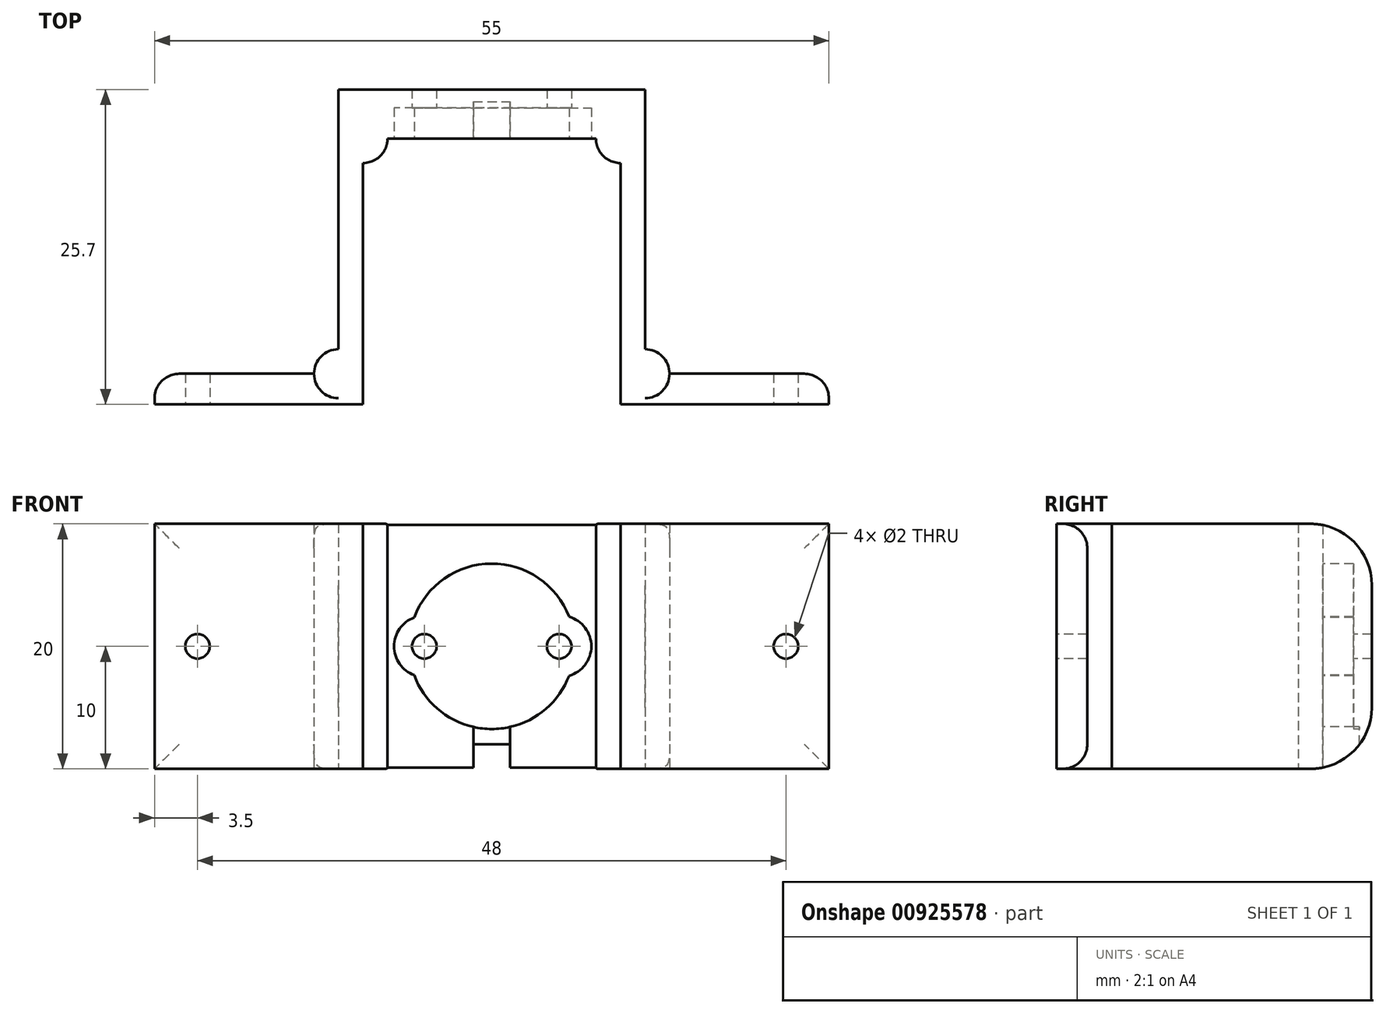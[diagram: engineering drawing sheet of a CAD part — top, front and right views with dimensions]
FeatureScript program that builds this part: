
annotation { "Feature Type Name" : "Feature", "Feature Type Description" : "" }
export const myFeature = defineFeature(function(context is Context, id is Id, definition is map)
    precondition{}
    {
        {
            var Q0;
            Q0=qCreatedBy(makeId("Front.planeOp"),FACE);
            var sketch = newSketch(context, id + "F0", { "sketchPlane" : qUnion([Q0])});
            skLineSegment(sketch, "E0.bottom", {"start": v(12.5, -10) * mm, "end": v(-12.5, -10) * mm});
            skLineSegment(sketch, "E0.top", {"start": v(12.5, 10) * mm, "end": v(-12.5, 10) * mm});
            skLineSegment(sketch, "E0.left", {"start": v(12.5, -10) * mm, "end": v(12.5, 10) * mm});
            skLineSegment(sketch, "E0.right", {"start": v(-12.5, -10) * mm, "end": v(-12.5, 10) * mm});
            skPoint(sketch, "E0.middle", {"position": v(0, 0) * mm});
            skSolve(sketch);
        }
        {
            var Q0;
            Q0=makeQuery(id+"F0.imprint","IMPRINT",FACE,{"disambiguationData":[TD([[makeQuery(id+"F0.imprint","IMPRINT",EDGE,{"derivedFrom":sQuery(id+"F0.wireOp",EDGE,"E0.bottom")}),-1.0]])]});
            extrude(context, id + "F1", {"entities" : qUnion([Q0]), "depth" : 4 * mm, "offsetDistance" : 25 * mm});
        }
        {
            var Q0;
            Q0=makeQuery(id+"F1.opExtrude","CAP_FACE",FACE,{"disambiguationData":[OSD([sQuery(id+"F0.wireOp",EDGE,"E0.bottom"),sQuery(id+"F0.wireOp",EDGE,"E0.top"),sQuery(id+"F0.wireOp",EDGE,"E0.left"),sQuery(id+"F0.wireOp",EDGE,"E0.right")])],"isStart":false});
            var sketch = newSketch(context, id + "F2", { "sketchPlane" : qUnion([Q0])});
            skCircle(sketch, "E1", {"center": v(0, 0) * mm, "radius": 6.75 * mm});
            skSolve(sketch);
        }
        {
            var Q0;
            Q0 = qSketchRegion(id + "F2", true);
            extrude(context, id + "F3", {"entities" : qUnion([Q0]), "operationType" : NewBodyOperationType.REMOVE, "oppositeDirection" : true, "depth" : 2.5 * mm, "offsetDistance" : 25 * mm});
        }
        {
            var Q0;
            Q0=makeQuery(id+"F1.opExtrude","CAP_FACE",FACE,{"disambiguationData":[OSD([sQuery(id+"F0.wireOp",EDGE,"E0.bottom"),sQuery(id+"F0.wireOp",EDGE,"E0.top"),sQuery(id+"F0.wireOp",EDGE,"E0.left"),sQuery(id+"F0.wireOp",EDGE,"E0.right")])],"isStart":false});
            var sketch = newSketch(context, id + "F4", { "sketchPlane" : qUnion([Q0])});
            skLineSegment(sketch, "E2.bottom", {"start": v(1.5, -11.91) * mm, "end": v(-1.5, -11.91) * mm});
            skLineSegment(sketch, "E2.top", {"start": v(1.5, -1.59) * mm, "end": v(-1.5, -1.59) * mm});
            skLineSegment(sketch, "E2.left", {"start": v(1.5, -11.91) * mm, "end": v(1.5, -1.59) * mm});
            skLineSegment(sketch, "E2.right", {"start": v(-1.5, -11.91) * mm, "end": v(-1.5, -1.59) * mm});
            skPoint(sketch, "E2.middle", {"position": v(0, -6.75) * mm});
            skPoint(sketch, "E2.middle.positionSnap0", {"position": v(0, -10) * mm});
            skPoint(sketch, "E2.centerSnap0", {"position": v(0, -10) * mm});
            skSolve(sketch);
        }
        {
            var Q0;
            {var subQ0=sQuery(id+"F4.wireOp",EDGE,"E2.left");var subQ1=makeQuery(id+"F1.opExtrude","CAP_EDGE",EDGE,{"disambiguationData":[OSD([sQuery(id+"F0.wireOp",EDGE,"E0.bottom")])],"isStart":false});var subQ2=makeQuery(id+"F4.imprint","INTERSECT",VERTEX,{"derivedFrom":[subQ1,subQ0]});Q0=makeQuery(id+"F4.imprint","IMPRINT",FACE,{"disambiguationData":[TD([[makeQuery(id+"F4.imprint","IMPRINT",EDGE,{"disambiguationData":[TD([[subQ2,-1.0]])],"derivedFrom":subQ0}),1.0]])]});}
            extrude(context, id + "F5", {"entities" : qUnion([Q0]), "operationType" : NewBodyOperationType.REMOVE, "oppositeDirection" : true, "depth" : 3 * mm, "offsetDistance" : 25 * mm});
        }
        {
            var Q0;
            Q0=makeQuery(id+"F3.boolean.opBoolean","COPY",FACE,{"derivedFrom":makeQuery(id+"F3.opExtrude","CAP_FACE",FACE,{"disambiguationData":[OSD([sQuery(id+"F2.wireOp",EDGE,"E1")])],"isStart":false})});
            var sketch = newSketch(context, id + "F6", { "sketchPlane" : qUnion([Q0])});
            skLineSegment(sketch, "E3", {"start": v(0, 0) * mm, "end": v(5.5, 0) * mm});
            skLineSegment(sketch, "E4", {"start": v(5.5, 0) * mm, "end": v(-5.5, 0) * mm});
            skCircle(sketch, "E5", {"center": v(-5.5, 0) * mm, "radius": 1 * mm});
            skCircle(sketch, "E6", {"center": v(5.5, 0) * mm, "radius": 1 * mm});
            skSolve(sketch);
        }
        {
            var Q0;
            Q0=makeQuery(id+"F6.imprint","IMPRINT",FACE,{"disambiguationData":[TD([[makeQuery(id+"F6.imprint","IMPRINT",EDGE,{"derivedFrom":sQuery(id+"F6.wireOp",EDGE,"E5")}),1.0]])]});
            var Q1;
            Q1=makeQuery(id+"F6.imprint","IMPRINT",FACE,{"disambiguationData":[TD([[makeQuery(id+"F6.imprint","IMPRINT",EDGE,{"derivedFrom":sQuery(id+"F6.wireOp",EDGE,"E6")}),1.0]])]});
            extrude(context, id + "F7", {"entities" : qUnion([Q0, Q1]), "operationType" : NewBodyOperationType.REMOVE, "oppositeDirection" : true, "depth" : 25 * mm, "offsetDistance" : 25 * mm});
        }
        {
            var Q0;
            Q0=makeQuery(id+"F1.opExtrude","CAP_FACE",FACE,{"disambiguationData":[OSD([sQuery(id+"F0.wireOp",EDGE,"E0.bottom"),sQuery(id+"F0.wireOp",EDGE,"E0.top"),sQuery(id+"F0.wireOp",EDGE,"E0.left"),sQuery(id+"F0.wireOp",EDGE,"E0.right")])],"isStart":false});
            var sketch = newSketch(context, id + "F8", { "sketchPlane" : qUnion([Q0])});
            skCircle(sketch, "E7", {"center": v(-5.47, 0) * mm, "radius": 2.5 * mm});
            skCircle(sketch, "E8", {"center": v(5.62, 0) * mm, "radius": 2.5 * mm});
            skSolve(sketch);
        }
        {
            var Q0;
            {var subQ0=sQuery(id+"F8.wireOp",EDGE,"E7");var subQ1=makeQuery(id+"F3.boolean.opBoolean","COPY",EDGE,{"derivedFrom":makeQuery(id+"F3.opExtrude","CAP_EDGE",EDGE,{"disambiguationData":[OSD([sQuery(id+"F2.wireOp",EDGE,"E1")])],"isStart":true})});var subQ2=makeQuery(id+"F8.imprint","INTERSECT",VERTEX,{"disambiguationData":[OD(0.0)],"derivedFrom":[subQ1,subQ0]});Q0=makeQuery(id+"F8.imprint","IMPRINT",FACE,{"disambiguationData":[TD([[makeQuery(id+"F8.imprint","IMPRINT",EDGE,{"disambiguationData":[TD([[subQ2,1.0]])],"derivedFrom":subQ0}),1.0]])]});}
            var Q1;
            {var subQ0=sQuery(id+"F8.wireOp",EDGE,"E8");var subQ1=makeQuery(id+"F3.boolean.opBoolean","COPY",EDGE,{"derivedFrom":makeQuery(id+"F3.opExtrude","CAP_EDGE",EDGE,{"disambiguationData":[OSD([sQuery(id+"F2.wireOp",EDGE,"E1")])],"isStart":true})});var subQ2=makeQuery(id+"F8.imprint","INTERSECT",VERTEX,{"disambiguationData":[OD(0.0)],"derivedFrom":[subQ1,subQ0]});Q1=makeQuery(id+"F8.imprint","IMPRINT",FACE,{"disambiguationData":[TD([[makeQuery(id+"F8.imprint","IMPRINT",EDGE,{"disambiguationData":[TD([[subQ2,-1.0]])],"derivedFrom":subQ0}),1.0]])]});}
            extrude(context, id + "F9", {"entities" : qUnion([Q0, Q1]), "operationType" : NewBodyOperationType.REMOVE, "oppositeDirection" : true, "depth" : 2.5 * mm, "offsetDistance" : 25 * mm});
        }
        {
            var Q0;
            Q0=makeQuery(id+"F1.opExtrude","CAP_FACE",FACE,{"disambiguationData":[OSD([sQuery(id+"F0.wireOp",EDGE,"E0.bottom"),sQuery(id+"F0.wireOp",EDGE,"E0.top"),sQuery(id+"F0.wireOp",EDGE,"E0.left"),sQuery(id+"F0.wireOp",EDGE,"E0.right")])],"isStart":false});
            var sketch = newSketch(context, id + "F10", { "sketchPlane" : qUnion([Q0])});
            skLineSegment(sketch, "E9.bottom", {"start": v(-12.5, 10) * mm, "end": v(-10.5, 10) * mm});
            skLineSegment(sketch, "E9.top", {"start": v(-12.5, -10) * mm, "end": v(-10.5, -10) * mm});
            skLineSegment(sketch, "E9.left", {"start": v(-12.5, 10) * mm, "end": v(-12.5, -10) * mm});
            skLineSegment(sketch, "E9.right", {"start": v(-10.5, 10) * mm, "end": v(-10.5, -10) * mm});
            skLineSegment(sketch, "E10.bottom", {"start": v(12.5, 10) * mm, "end": v(10.5, 10) * mm});
            skLineSegment(sketch, "E10.top", {"start": v(12.5, -10) * mm, "end": v(10.5, -10) * mm});
            skLineSegment(sketch, "E10.left", {"start": v(12.5, 10) * mm, "end": v(12.5, -10) * mm});
            skLineSegment(sketch, "E10.right", {"start": v(10.5, 10) * mm, "end": v(10.5, -10) * mm});
            skSolve(sketch);
        }
        {
            var Q0;
            Q0=makeQuery(id+"F10.imprint","IMPRINT",FACE,{"disambiguationData":[TD([[makeQuery(id+"F10.imprint","IMPRINT",EDGE,{"derivedFrom":sQuery(id+"F10.wireOp",EDGE,"E9.bottom")}),1.0]])]});
            var Q1;
            Q1=makeQuery(id+"F10.imprint","IMPRINT",FACE,{"disambiguationData":[TD([[makeQuery(id+"F10.imprint","IMPRINT",EDGE,{"derivedFrom":sQuery(id+"F10.wireOp",EDGE,"E10.bottom")}),1.0]])]});
            extrude(context, id + "F11", {"entities" : qUnion([Q0, Q1]), "operationType" : NewBodyOperationType.ADD, "depth" : 21.7 * mm, "offsetDistance" : 25 * mm});
        }
        {
            var Q0;
            Q0=makeQuery(id+"F11.boolean.opBoolean","MERGE",FACE,{"derivedFrom":[makeQuery(id+"F1.opExtrude","SWEPT_FACE",FACE,{"disambiguationData":[OSD([sQuery(id+"F0.wireOp",EDGE,"E0.left")])]}),makeQuery(id+"F11.opExtrude","SWEPT_FACE",FACE,{"disambiguationData":[OSD([sQuery(id+"F10.wireOp",EDGE,"E10.left")])]})]});
            var sketch = newSketch(context, id + "F12", { "sketchPlane" : qUnion([Q0])});
            skLineSegment(sketch, "E11.bottom", {"start": v(-25.7, -10) * mm, "end": v(-23.2, -10) * mm});
            skLineSegment(sketch, "E11.top", {"start": v(-25.7, 10) * mm, "end": v(-23.2, 10) * mm});
            skLineSegment(sketch, "E11.left", {"start": v(-25.7, -10) * mm, "end": v(-25.7, 10) * mm});
            skLineSegment(sketch, "E11.right", {"start": v(-23.2, -10) * mm, "end": v(-23.2, 10) * mm});
            skSolve(sketch);
        }
        {
            var Q0;
            Q0 = qSketchRegion(id + "F12", true);
            extrude(context, id + "F13", {"entities" : qUnion([Q0]), "operationType" : NewBodyOperationType.ADD, "depth" : 15 * mm, "offsetDistance" : 25 * mm});
        }
        {
            var Q0;
            Q0=makeQuery(id+"F11.boolean.opBoolean","MERGE",FACE,{"derivedFrom":[makeQuery(id+"F1.opExtrude","SWEPT_FACE",FACE,{"disambiguationData":[OSD([sQuery(id+"F0.wireOp",EDGE,"E0.right")])]}),makeQuery(id+"F11.opExtrude","SWEPT_FACE",FACE,{"disambiguationData":[OSD([sQuery(id+"F10.wireOp",EDGE,"E9.left")])]})]});
            var sketch = newSketch(context, id + "F14", { "sketchPlane" : qUnion([Q0])});
            skLineSegment(sketch, "E12.bottom", {"start": v(25.7, 10) * mm, "end": v(23.2, 10) * mm});
            skLineSegment(sketch, "E12.top", {"start": v(25.7, -10) * mm, "end": v(23.2, -10) * mm});
            skLineSegment(sketch, "E12.left", {"start": v(25.7, 10) * mm, "end": v(25.7, -10) * mm});
            skLineSegment(sketch, "E12.right", {"start": v(23.2, 10) * mm, "end": v(23.2, -10) * mm});
            skSolve(sketch);
        }
        {
            var Q0;
            Q0 = qSketchRegion(id + "F14", true);
            extrude(context, id + "F15", {"entities" : qUnion([Q0]), "operationType" : NewBodyOperationType.ADD, "depth" : 15 * mm, "offsetDistance" : 25 * mm});
        }
        {
            var Q0;
            Q0=makeQuery(id+"F15.boolean.opBoolean","MERGE",FACE,{"derivedFrom":[makeQuery(id+"F13.boolean.opBoolean","MERGE",FACE,{"derivedFrom":[makeQuery(id+"F11.boolean.opBoolean","MERGE",FACE,{"derivedFrom":[makeQuery(id+"F1.opExtrude","SWEPT_FACE",FACE,{"disambiguationData":[OSD([sQuery(id+"F0.wireOp",EDGE,"E0.bottom")])]}),makeQuery(id+"F11.opExtrude","SWEPT_FACE",FACE,{"disambiguationData":[OSD([sQuery(id+"F10.wireOp",EDGE,"E9.top")])]}),makeQuery(id+"F11.opExtrude","SWEPT_FACE",FACE,{"disambiguationData":[OSD([sQuery(id+"F10.wireOp",EDGE,"E10.top")])]})]}),makeQuery(id+"F13.opExtrude","SWEPT_FACE",FACE,{"disambiguationData":[OSD([sQuery(id+"F12.wireOp",EDGE,"E11.bottom")])]})]}),makeQuery(id+"F15.opExtrude","SWEPT_FACE",FACE,{"disambiguationData":[OSD([sQuery(id+"F14.wireOp",EDGE,"E12.top")])]})]});
            var sketch = newSketch(context, id + "F16", { "sketchPlane" : qUnion([Q0])});
            skCircle(sketch, "E13", {"center": v(-12.5, 23.2) * mm, "radius": 2 * mm});
            skCircle(sketch, "E14", {"center": v(12.5, 23.2) * mm, "radius": 2 * mm});
            skCircle(sketch, "E15", {"center": v(-10.5, 4) * mm, "radius": 2 * mm});
            skCircle(sketch, "E16", {"center": v(10.5, 4) * mm, "radius": 2 * mm});
            skSolve(sketch);
        }
        {
            var Q0;
            Q0 = qSketchRegion(id + "F16", true);
            extrude(context, id + "F17", {"entities" : qUnion([Q0]), "operationType" : NewBodyOperationType.ADD, "oppositeDirection" : true, "depth" : 20 * mm, "offsetDistance" : 25 * mm});
        }
        {
            var Q0;
            Q0=makeQuery(id+"F1.opExtrude","CAP_EDGE",EDGE,{"disambiguationData":[OSD([sQuery(id+"F0.wireOp",EDGE,"E0.top")])],"isStart":true});
            var Q1;
            Q1=makeQuery(id+"F1.opExtrude","CAP_EDGE",EDGE,{"disambiguationData":[OSD([sQuery(id+"F0.wireOp",EDGE,"E0.bottom")])],"isStart":true});
            fillet(context, id + "F18", {"entities" : qUnion([Q0, Q1]), "radius" : 5 * mm, "tangentPropagation" : true, "allowEdgeOverflow" : false});
        }
        {
            var Q0;
            Q0=makeQuery(id+"F13.opExtrude","SWEPT_EDGE",EDGE,{"disambiguationData":[OSD([sQuery(id+"F0.wireOp",EDGE,"E0.bottom"),sQuery(id+"F0.wireOp",EDGE,"E0.left"),sQuery(id+"F10.wireOp",EDGE,"E10.top"),sQuery(id+"F10.wireOp",EDGE,"E10.left"),sQuery(id+"F12.wireOp",EDGE,"E11.bottom"),sQuery(id+"F12.wireOp",EDGE,"E11.right")])]});
            var Q1;
            Q1=makeQuery(id+"F13.opExtrude","SWEPT_EDGE",EDGE,{"disambiguationData":[OSD([sQuery(id+"F0.wireOp",EDGE,"E0.top"),sQuery(id+"F0.wireOp",EDGE,"E0.left"),sQuery(id+"F10.wireOp",EDGE,"E10.bottom"),sQuery(id+"F10.wireOp",EDGE,"E10.left"),sQuery(id+"F12.wireOp",EDGE,"E11.top"),sQuery(id+"F12.wireOp",EDGE,"E11.right")])]});
            var Q2;
            Q2=makeQuery(id+"F15.opExtrude","SWEPT_EDGE",EDGE,{"disambiguationData":[OSD([sQuery(id+"F0.wireOp",EDGE,"E0.bottom"),sQuery(id+"F0.wireOp",EDGE,"E0.right"),sQuery(id+"F10.wireOp",EDGE,"E9.top"),sQuery(id+"F10.wireOp",EDGE,"E9.left"),sQuery(id+"F14.wireOp",EDGE,"E12.top"),sQuery(id+"F14.wireOp",EDGE,"E12.right")])]});
            var Q3;
            Q3=makeQuery(id+"F15.opExtrude","SWEPT_EDGE",EDGE,{"disambiguationData":[OSD([sQuery(id+"F0.wireOp",EDGE,"E0.top"),sQuery(id+"F0.wireOp",EDGE,"E0.right"),sQuery(id+"F10.wireOp",EDGE,"E9.bottom"),sQuery(id+"F10.wireOp",EDGE,"E9.left"),sQuery(id+"F14.wireOp",EDGE,"E12.bottom"),sQuery(id+"F14.wireOp",EDGE,"E12.right")])]});
            var Q4;
            Q4=makeQuery(id+"F13.opExtrude","CAP_EDGE",EDGE,{"disambiguationData":[OSD([sQuery(id+"F12.wireOp",EDGE,"E11.right")])],"isStart":false});
            var Q5;
            Q5=makeQuery(id+"F15.opExtrude","CAP_EDGE",EDGE,{"disambiguationData":[OSD([sQuery(id+"F14.wireOp",EDGE,"E12.right")])],"isStart":false});
            fillet(context, id + "F19", {"entities" : qUnion([Q0, Q1, Q2, Q3, Q4, Q5]), "radius" : 2 * mm, "tangentPropagation" : true, "allowEdgeOverflow" : false});
        }
        {
            var Q0;
            Q0=makeQuery(id+"F13.boolean.opBoolean","MERGE",FACE,{"derivedFrom":[makeQuery(id+"F11.opExtrude","CAP_FACE",FACE,{"disambiguationData":[OSD([sQuery(id+"F10.wireOp",EDGE,"E10.bottom"),sQuery(id+"F10.wireOp",EDGE,"E10.top"),sQuery(id+"F10.wireOp",EDGE,"E10.left"),sQuery(id+"F10.wireOp",EDGE,"E10.right")])],"isStart":false}),makeQuery(id+"F13.opExtrude","SWEPT_FACE",FACE,{"disambiguationData":[OSD([sQuery(id+"F12.wireOp",EDGE,"E11.left")])]})]});
            var sketch = newSketch(context, id + "F20", { "sketchPlane" : qUnion([Q0])});
            skLineSegment(sketch, "E17", {"start": v(0, 0) * mm, "end": v(24, 0) * mm});
            skPoint(sketch, "E17.endSnap0", {"position": v(27.5, 0) * mm});
            skLineSegment(sketch, "E18", {"start": v(24, 0) * mm, "end": v(-24, 0) * mm});
            skCircle(sketch, "E19", {"center": v(-24, 0) * mm, "radius": 1 * mm});
            skCircle(sketch, "E20", {"center": v(24, 0) * mm, "radius": 1 * mm});
            skSolve(sketch);
        }
        {
            var Q0;
            Q0=makeQuery(id+"F20.imprint","IMPRINT",FACE,{"disambiguationData":[TD([[makeQuery(id+"F20.imprint","IMPRINT",EDGE,{"derivedFrom":sQuery(id+"F20.wireOp",EDGE,"E19")}),1.0]])]});
            var Q1;
            Q1=makeQuery(id+"F20.imprint","IMPRINT",FACE,{"disambiguationData":[TD([[makeQuery(id+"F20.imprint","IMPRINT",EDGE,{"derivedFrom":sQuery(id+"F20.wireOp",EDGE,"E20")}),1.0]])]});
            extrude(context, id + "F21", {"entities" : qUnion([Q0, Q1]), "operationType" : NewBodyOperationType.REMOVE, "oppositeDirection" : true, "depth" : 25 * mm, "offsetDistance" : 25 * mm});
        }
    });
